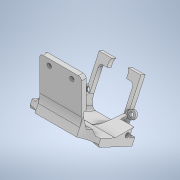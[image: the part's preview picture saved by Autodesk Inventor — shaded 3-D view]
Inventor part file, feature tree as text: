
AUTODESK INVENTOR PART (.ipt)
format: ipt  version: 2022 (Build 260153070, 153G)  size: 433,152 bytes
history: native  units: mm
features: extrude x12, sketch x9, fillet x6, plane x1, mirror x1, projected_geometry x1
ambient origin geometry x8: Origin, YZ Plane, XZ Plane, XY Plane, X Axis, Y Axis, Z Axis, Center Point
bodies: Solid1 (feature_tree)
feature tree (30):
  extrude  "Extrusion1"  Depth=14.5mm
  extrude  "Extrusion2"  Depth=33.0mm
  extrude  "Extrusion3"  Depth=3.75mm
  extrude  "Extrusion4"  Depth=4.363323mm
  fillet  "Fillet1"  Radius=7.5mm
  extrude  "Extrusion5"  Depth=28.0mm
  extrude  "Extrusion6"  Depth=9.1mm
  sketch  "Sketch7"  dims[d16=2.4mm d17=7.35mm]
  extrude  "Extrusion7"  Depth=7.35mm
  plane  "Work Plane1"
  extrude  "Extrusion8"  Depth=7.0mm
  mirror  "Mirror1"
  fillet  "Fillet2"  Radius=19.5mm
  fillet  "Fillet3"  Radius=11.0mm
  fillet  "Fillet4"  Radius=13.65mm
  fillet  "Fillet5"  Radius=2.7mm
  fillet  "Fillet6"  Radius=11.2mm
  sketch  "Sketch8"  dims[d18=3.0mm d19=0.0mm d20=7.0mm d22=19.5mm d23=0.0mm d25=11.0mm d26=13.65mm d27=2.7mm d28=11.2mm]
  extrude  "Extrusion9"  Depth=1.5mm
  extrude  "Extrusion10"  Depth=1.5mm
  extrude  "Extrusion11"  Depth=1.5mm
  extrude  "Extrusion12"  Depth=8.6mm
  sketch  "Sketch1"  dims[d0=2.7mm d1=14.5mm]
  sketch  "Sketch2"  dims[d3=2.0mm d4=33.0mm]
  sketch  "Sketch3"  dims[d5=26.75mm d6=3.75mm]
  sketch  "Sketch4"  dims[d8=3.0mm d9=0.0mm d10=4.363323mm d11=7.5mm]
  sketch  "Sketch5"  dims[d12=2.7mm d13=28.0mm]
  sketch  "Sketch6"  dims[d14=3.0mm d15=9.1mm]
  projected_geometry  "Projected Loop1"
  sketch  "Sketch9"  dims[d29=1.8mm d30=0.0mm d31=12.0mm d32=2.7mm d36=9.25mm d37=8.6mm d38=2.5mm d39=2.5mm d40=54.2mm d41=27.1mm d42=7.0mm d43=24.2mm d44=3.475mm d45=4.125mm d46=3.0mm d47=0.0mm d48=1.5mm d49=0.0mm d50=2.7mm d51=2.397mm d52=8.895mm d53=2.0mm d54=8.6mm d55=0.0mm d56=8.6mm d57=0.0mm d58=12.0mm d59=12.0mm d60=12.0mm d61=12.0mm d62=12.0mm d63=30.0mm d64=2.0mm d65=15.0mm d66=3.0mm d67=0.0mm d68=12.6mm d69=1.5mm d70=2.7mm d71=28.0mm d72=21.26mm d73=5.0mm d74=3.0mm d75=0.0mm d76=1.5mm d77=0.0mm d78=1.5mm d79=0.0mm]
